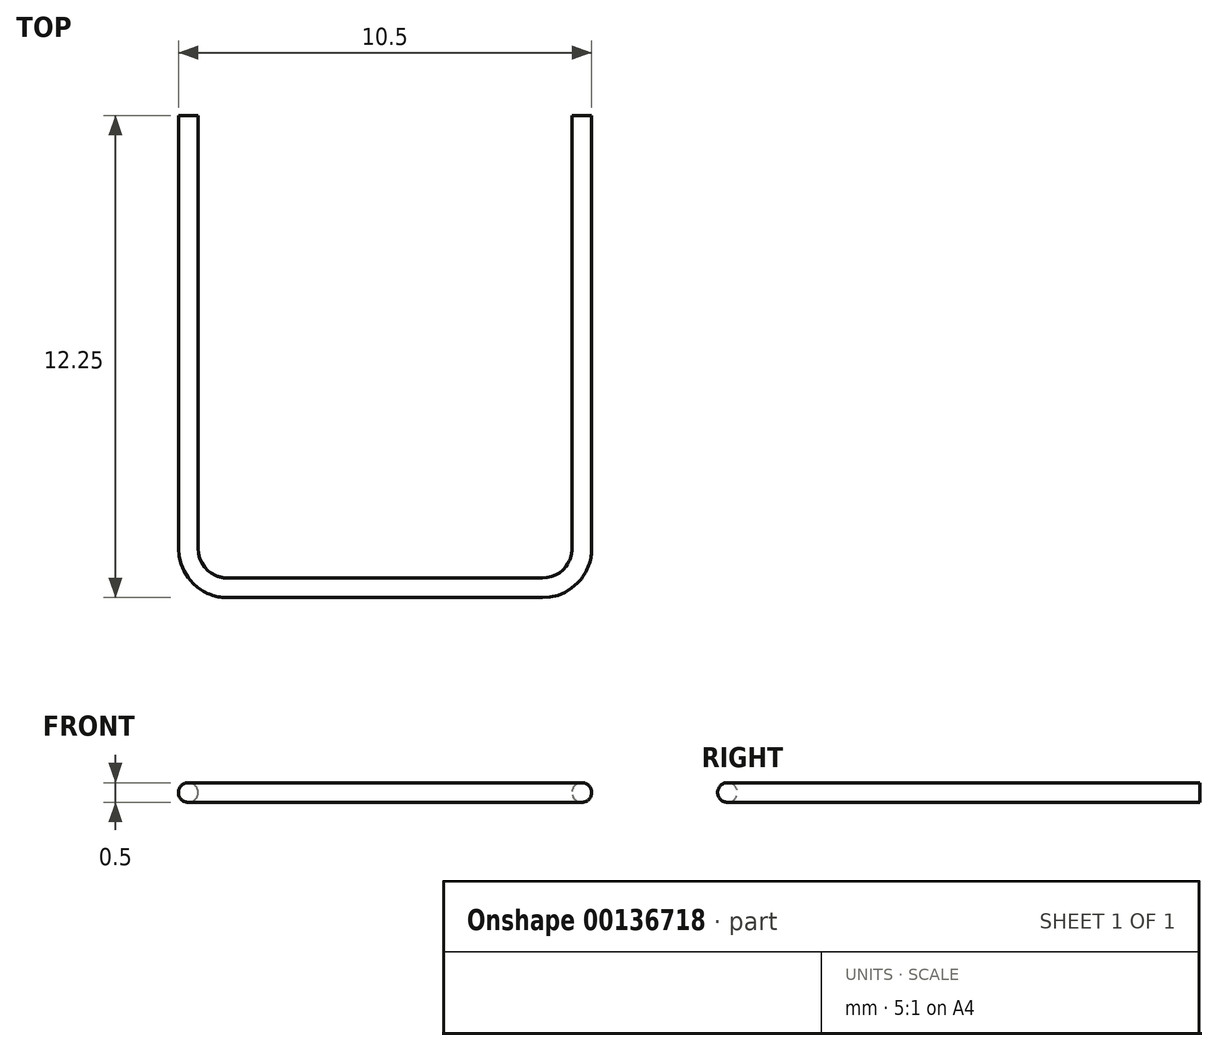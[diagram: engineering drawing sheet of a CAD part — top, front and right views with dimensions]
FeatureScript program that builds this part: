
annotation { "Feature Type Name" : "Feature", "Feature Type Description" : "" }
export const myFeature = defineFeature(function(context is Context, id is Id, definition is map)
    precondition{}
    {
        {
            var Q0;
            Q0=qCreatedBy(makeId("Top.planeOp"),FACE);
            var sketch = newSketch(context, id + "F0", { "sketchPlane" : qUnion([Q0])});
            skLineSegment(sketch, "E0.top", {"start": v(4, -6) * mm, "end": v(-4, -6) * mm});
            skLineSegment(sketch, "E0.left", {"start": v(5, 6) * mm, "end": v(5, -5) * mm});
            skLineSegment(sketch, "E0.right", {"start": v(-5, 6) * mm, "end": v(-5, -5) * mm});
            skPoint(sketch, "E0.middle", {"position": v(0, 0) * mm});
            skPoint(sketch, "E1.visualSharp", {"position": v(-5, -6) * mm});
            skArc(sketch, "E1.filletArc", {"start": v(-5, -5) * mm, "mid": v(-4.7, -5.7) * mm, "end": v(-4, -6) * mm});
            skPoint(sketch, "E2.visualSharp", {"position": v(5, -6) * mm});
            skArc(sketch, "E2.filletArc", {"start": v(4, -6) * mm, "mid": v(4.7, -5.7) * mm, "end": v(5, -5) * mm});
            skPoint(sketch, "E3", {"position": v(-5, 6) * mm});
            skSolve(sketch);
        }
        {
            var Q0;
            Q0=sQuery(id+"F0.wireOp",VERTEX,"E0.right.start");
            var Q1;
            Q1=qCreatedBy(makeId("Front.planeOp"),FACE);
            cPlane(context, id + "F1", {"entities" : qUnion([Q0, Q1]), "cplaneType" : CPlaneType.PLANE_POINT, "offset" : 25 * mm, "width" : 150 * mm, "height" : 150 * mm});
        }
        {
            var Q0;
            Q0=qCreatedBy(id+"F1.planeOp",FACE);
            var sketch = newSketch(context, id + "F2", { "sketchPlane" : qUnion([Q0])});
            skCircle(sketch, "E4", {"center": v(-5, 0) * mm, "radius": 0.25 * mm});
            skSolve(sketch);
        }
        {
            var Q0;
            Q0=makeQuery(id+"F2.imprint","IMPRINT",FACE,{"disambiguationData":[TD([[makeQuery(id+"F2.imprint","IMPRINT",EDGE,{"derivedFrom":sQuery(id+"F2.wireOp",EDGE,"E4")}),1.0]])]});
            var Q1;
            Q1=sQuery(id+"F0.wireOp",EDGE,"E0.right");
            var Q2;
            Q2=sQuery(id+"F0.wireOp",EDGE,"E1.filletArc");
            var Q3;
            Q3=sQuery(id+"F0.wireOp",EDGE,"E0.top");
            var Q4;
            Q4=sQuery(id+"F0.wireOp",EDGE,"E2.filletArc");
            var Q5;
            Q5=sQuery(id+"F0.wireOp",EDGE,"E0.left");
            sweep(context, id + "F3", {"profiles" : qUnion([Q0]), "path" : qUnion([Q1, Q2, Q3, Q4, Q5])});
        }
    });
